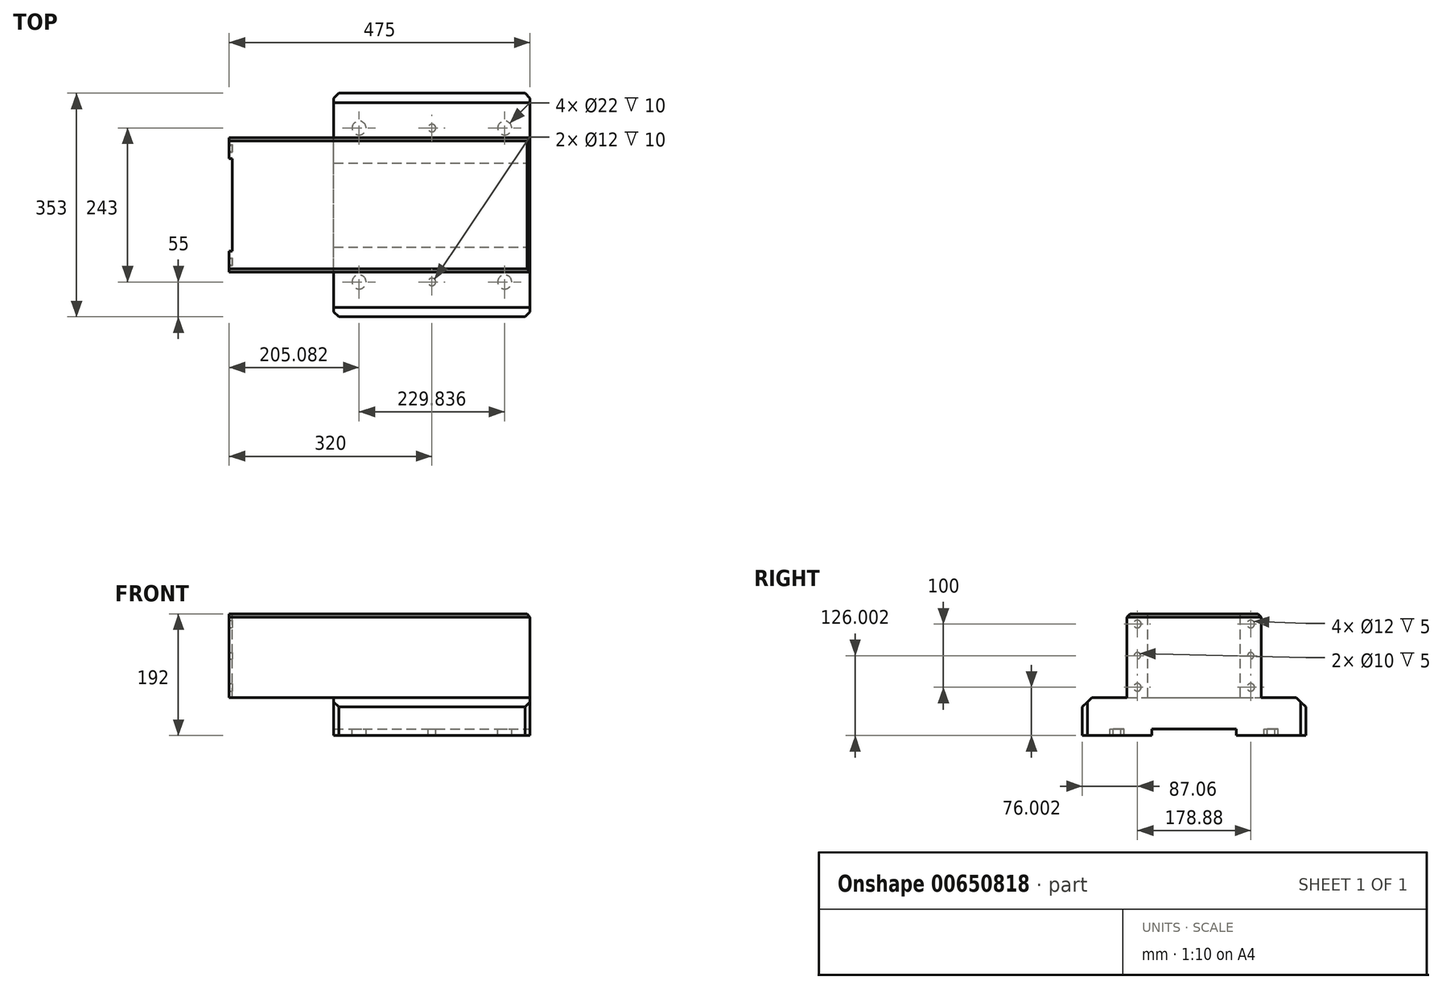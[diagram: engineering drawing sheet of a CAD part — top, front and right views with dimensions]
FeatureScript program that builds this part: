
annotation { "Feature Type Name" : "Feature", "Feature Type Description" : "" }
export const myFeature = defineFeature(function(context is Context, id is Id, definition is map)
    precondition{}
    {
        {
            var Q0;
            Q0=qCreatedBy(makeId("Right.planeOp"),FACE);
            var sketch = newSketch(context, id + "F0", { "sketchPlane" : qUnion([Q0])});
            skLineSegment(sketch, "E0.bottom", {"start": v(-105.91, 36.32) * mm, "end": v(105.91, 36.32) * mm});
            skLineSegment(sketch, "E0.top", {"start": v(-105.91, -95.68) * mm, "end": v(105.91, -95.68) * mm});
            skLineSegment(sketch, "E0.left", {"start": v(-105.91, 36.32) * mm, "end": v(-105.91, -95.68) * mm});
            skLineSegment(sketch, "E0.right", {"start": v(105.92, 36.32) * mm, "end": v(105.92, -95.68) * mm});
            skLineSegment(sketch, "E1", {"start": v(0, 36.32) * mm, "end": v(0, -95.68) * mm, "construction": true});
            skSolve(sketch);
        }
        {
            var Q0;
            Q0 = qSketchRegion(id + "F0", true);
            extrude(context, id + "F1", {"entities" : qUnion([Q0]), "depth" : 310 * mm, "offsetDistance" : 25 * mm, "hasSecondDirection" : true, "secondDirectionOppositeDirection" : true, "secondDirectionDepth" : 160 * mm});
        }
        {
            var Q0;
            Q0=makeQuery(id+"F1.opExtrude","CAP_FACE",FACE,{"disambiguationData":[OSD([sQuery(id+"F0.wireOp",EDGE,"E0.bottom"),sQuery(id+"F0.wireOp",EDGE,"E0.top"),sQuery(id+"F0.wireOp",EDGE,"E0.left"),sQuery(id+"F0.wireOp",EDGE,"E0.right")])],"isStart":true});
            var sketch = newSketch(context, id + "F2", { "sketchPlane" : qUnion([Q0])});
            skLineSegment(sketch, "E2.bottom", {"start": v(-105.92, -95.68) * mm, "end": v(-72.97, -95.68) * mm});
            skLineSegment(sketch, "E2.top", {"start": v(-105.92, 36.32) * mm, "end": v(-72.97, 36.32) * mm});
            skLineSegment(sketch, "E2.left", {"start": v(-105.92, -95.68) * mm, "end": v(-105.92, 36.32) * mm});
            skLineSegment(sketch, "E2.right", {"start": v(-72.97, -95.68) * mm, "end": v(-72.97, 36.32) * mm});
            skCircle(sketch, "E3", {"center": v(-89.44, 20.32) * mm, "radius": 6 * mm});
            skCircle(sketch, "E4", {"center": v(-89.44, -29.68) * mm, "radius": 5 * mm});
            skLineSegment(sketch, "E5", {"start": v(-89.44, 36.32) * mm, "end": v(-89.44, -132.2) * mm, "construction": true});
            skLineSegment(sketch, "E6", {"start": v(-105.92, -29.68) * mm, "end": v(-72.97, -29.68) * mm, "construction": true});
            skCircle(sketch, "E7.MirrorC", {"center": v(-89.44, -79.68) * mm, "radius": 6 * mm});
            skLineSegment(sketch, "E8", {"start": v(0, 0) * mm, "end": v(0, -157.18) * mm, "construction": true});
            skLineSegment(sketch, "E9.MirrorCS", {"start": v(89.44, 36.32) * mm, "end": v(89.44, -132.2) * mm, "construction": true});
            skLineSegment(sketch, "E10.MirrorCS", {"start": v(105.92, -95.68) * mm, "end": v(72.97, -95.68) * mm});
            skLineSegment(sketch, "E11.MirrorCS", {"start": v(105.91, 36.32) * mm, "end": v(72.96, 36.32) * mm});
            skLineSegment(sketch, "E12.MirrorCS", {"start": v(105.92, -95.68) * mm, "end": v(105.92, 36.32) * mm});
            skLineSegment(sketch, "E13.MirrorCS", {"start": v(105.92, -29.68) * mm, "end": v(72.97, -29.68) * mm, "construction": true});
            skLineSegment(sketch, "E14.MirrorCS", {"start": v(72.97, -95.68) * mm, "end": v(72.97, 36.32) * mm});
            skCircle(sketch, "E15.MirrorC", {"center": v(89.44, -79.68) * mm, "radius": 6 * mm});
            skCircle(sketch, "E16.MirrorC", {"center": v(89.44, -29.68) * mm, "radius": 5 * mm});
            skCircle(sketch, "E17.MirrorC", {"center": v(89.44, 20.32) * mm, "radius": 6 * mm});
            skSolve(sketch);
        }
        {
            var Q0;
            Q0 = qSketchRegion(id + "F2", true);
            extrude(context, id + "F3", {"entities" : qUnion([Q0]), "operationType" : NewBodyOperationType.ADD, "depth" : 5 * mm, "offsetDistance" : 25 * mm});
        }
        {
            var Q0;
            Q0=makeQuery(id+"F1.opExtrude","CAP_EDGE",EDGE,{"disambiguationData":[OSD([sQuery(id+"F0.wireOp",EDGE,"E0.bottom")])],"isStart":false});
            var Q1;
            Q1=makeQuery(id+"F1.opExtrude","SWEPT_EDGE",EDGE,{"disambiguationData":[OSD([sQuery(id+"F0.wireOp",EDGE,"E0.bottom"),sQuery(id+"F0.wireOp",EDGE,"E0.left")])]});
            var Q2;
            Q2=makeQuery(id+"F1.opExtrude","SWEPT_EDGE",EDGE,{"disambiguationData":[OSD([sQuery(id+"F0.wireOp",EDGE,"E0.bottom"),sQuery(id+"F0.wireOp",EDGE,"E0.right")])]});
            chamfer(context, id + "F4", {"entities" : qUnion([Q0, Q1, Q2]), "width" : 5 * mm, "tangentPropagation" : true});
        }
        {
            var Q0;
            Q0=makeQuery(id+"F3.boolean.opBoolean","MERGE",FACE,{"derivedFrom":[makeQuery(id+"F1.opExtrude","SWEPT_FACE",FACE,{"disambiguationData":[OSD([sQuery(id+"F0.wireOp",EDGE,"E0.top")])]}),makeQuery(id+"F3.opExtrude","SWEPT_FACE",FACE,{"disambiguationData":[OSD([sQuery(id+"F2.wireOp",EDGE,"E2.bottom")])]}),makeQuery(id+"F3.opExtrude","SWEPT_FACE",FACE,{"disambiguationData":[OSD([sQuery(id+"F2.wireOp",EDGE,"E10.MirrorCS")])]})]});
            var sketch = newSketch(context, id + "F5", { "sketchPlane" : qUnion([Q0])});
            skLineSegment(sketch, "E18", {"start": v(0, 0) * mm, "end": v(310, 0) * mm, "construction": true});
            skLineSegment(sketch, "E19.bottom", {"start": v(0, 176.5) * mm, "end": v(310, 176.5) * mm});
            skLineSegment(sketch, "E19.top", {"start": v(0, -176.5) * mm, "end": v(310, -176.5) * mm});
            skLineSegment(sketch, "E19.left", {"start": v(0, 176.5) * mm, "end": v(0, -176.5) * mm});
            skLineSegment(sketch, "E19.right", {"start": v(310, 176.5) * mm, "end": v(310, -176.5) * mm});
            skPoint(sketch, "E19.middle", {"position": v(155, 0) * mm});
            skSolve(sketch);
        }
        {
            var Q0;
            Q0 = qSketchRegion(id + "F5", true);
            extrude(context, id + "F6", {"entities" : qUnion([Q0]), "operationType" : NewBodyOperationType.ADD, "depth" : 50 * mm, "offsetDistance" : 25 * mm});
        }
        {
            var Q0;
            Q0=makeQuery(id+"F6.opExtrude","CAP_EDGE",EDGE,{"disambiguationData":[OSD([sQuery(id+"F5.wireOp",EDGE,"E19.bottom")])],"isStart":true});
            var Q1;
            Q1=makeQuery(id+"F6.opExtrude","CAP_EDGE",EDGE,{"disambiguationData":[OSD([sQuery(id+"F5.wireOp",EDGE,"E19.top")])],"isStart":true});
            chamfer(context, id + "F7", {"entities" : qUnion([Q0, Q1]), "width" : 15 * mm, "tangentPropagation" : true});
        }
        {
            var Q0;
            Q0=makeQuery(id+"F6.opExtrude","CAP_FACE",FACE,{"disambiguationData":[OSD([sQuery(id+"F5.wireOp",EDGE,"E19.bottom"),sQuery(id+"F5.wireOp",EDGE,"E19.top"),sQuery(id+"F5.wireOp",EDGE,"E19.left"),sQuery(id+"F5.wireOp",EDGE,"E19.right")])],"isStart":false});
            var sketch = newSketch(context, id + "F8", { "sketchPlane" : qUnion([Q0])});
            skLineSegment(sketch, "E20.bottom", {"start": v(0, 176.5) * mm, "end": v(310, 176.5) * mm});
            skLineSegment(sketch, "E20.top", {"start": v(0, 66.5) * mm, "end": v(310, 66.5) * mm});
            skLineSegment(sketch, "E20.left", {"start": v(0, 176.5) * mm, "end": v(0, 66.5) * mm});
            skLineSegment(sketch, "E20.right", {"start": v(310, 176.5) * mm, "end": v(310, 66.5) * mm});
            skLineSegment(sketch, "E21.MirrorCS", {"start": v(0, -66.5) * mm, "end": v(310, -66.5) * mm});
            skLineSegment(sketch, "E22.MirrorCS", {"start": v(0, -176.5) * mm, "end": v(310, -176.5) * mm});
            skLineSegment(sketch, "E23.MirrorCS", {"start": v(310, -176.5) * mm, "end": v(310, -66.5) * mm});
            skLineSegment(sketch, "E24.MirrorCS", {"start": v(0, -176.5) * mm, "end": v(0, -66.5) * mm});
            skCircle(sketch, "E25", {"center": v(40.08, 121.5) * mm, "radius": 11 * mm});
            skPoint(sketch, "E25.centerSnap0", {"position": v(0, 121.5) * mm});
            skCircle(sketch, "E26", {"center": v(155, 121.5) * mm, "radius": 6 * mm});
            skPoint(sketch, "E26.centerSnap0", {"position": v(155, 176.5) * mm});
            skLineSegment(sketch, "E27", {"start": v(155, 176.5) * mm, "end": v(155, 16.17) * mm, "construction": true});
            skCircle(sketch, "E28.MirrorC", {"center": v(269.92, 121.5) * mm, "radius": 11 * mm});
            skCircle(sketch, "E29.MirrorC", {"center": v(40.08, -121.5) * mm, "radius": 11 * mm});
            skCircle(sketch, "E30.MirrorC", {"center": v(155, -121.5) * mm, "radius": 6 * mm});
            skCircle(sketch, "E31.MirrorC", {"center": v(269.92, -121.5) * mm, "radius": 11 * mm});
            skSolve(sketch);
        }
        {
            var Q0;
            Q0 = qSketchRegion(id + "F8", true);
            extrude(context, id + "F9", {"entities" : qUnion([Q0]), "operationType" : NewBodyOperationType.ADD, "depth" : 10 * mm, "offsetDistance" : 25 * mm});
        }
        {
            var Q0;
            Q0=makeQuery(id+"F9.boolean.opBoolean","MERGE",EDGE,{"derivedFrom":[makeQuery(id+"F6.opExtrude","SWEPT_EDGE",EDGE,{"disambiguationData":[OSD([sQuery(id+"F5.wireOp",EDGE,"E19.bottom"),sQuery(id+"F5.wireOp",EDGE,"E19.left")])]}),makeQuery(id+"F9.opExtrude","SWEPT_EDGE",EDGE,{"disambiguationData":[OSD([sQuery(id+"F8.wireOp",EDGE,"E20.bottom"),sQuery(id+"F8.wireOp",EDGE,"E20.left")])]})]});
            var Q1;
            Q1=makeQuery(id+"F9.boolean.opBoolean","MERGE",EDGE,{"derivedFrom":[makeQuery(id+"F6.opExtrude","SWEPT_EDGE",EDGE,{"disambiguationData":[OSD([sQuery(id+"F5.wireOp",EDGE,"E19.top"),sQuery(id+"F5.wireOp",EDGE,"E19.left")])]}),makeQuery(id+"F9.opExtrude","SWEPT_EDGE",EDGE,{"disambiguationData":[OSD([sQuery(id+"F8.wireOp",EDGE,"E22.MirrorCS"),sQuery(id+"F8.wireOp",EDGE,"E24.MirrorCS")])]})]});
            var Q2;
            Q2=makeQuery(id+"F9.boolean.opBoolean","MERGE",EDGE,{"derivedFrom":[makeQuery(id+"F6.opExtrude","SWEPT_EDGE",EDGE,{"disambiguationData":[OSD([sQuery(id+"F5.wireOp",EDGE,"E19.top"),sQuery(id+"F5.wireOp",EDGE,"E19.right")])]}),makeQuery(id+"F9.opExtrude","SWEPT_EDGE",EDGE,{"disambiguationData":[OSD([sQuery(id+"F8.wireOp",EDGE,"E22.MirrorCS"),sQuery(id+"F8.wireOp",EDGE,"E23.MirrorCS")])]})]});
            var Q3;
            Q3=makeQuery(id+"F9.boolean.opBoolean","MERGE",EDGE,{"derivedFrom":[makeQuery(id+"F6.opExtrude","SWEPT_EDGE",EDGE,{"disambiguationData":[OSD([sQuery(id+"F5.wireOp",EDGE,"E19.bottom"),sQuery(id+"F5.wireOp",EDGE,"E19.right")])]}),makeQuery(id+"F9.opExtrude","SWEPT_EDGE",EDGE,{"disambiguationData":[OSD([sQuery(id+"F8.wireOp",EDGE,"E20.bottom"),sQuery(id+"F8.wireOp",EDGE,"E20.right")])]})]});
            chamfer(context, id + "F10", {"entities" : qUnion([Q0, Q1, Q2, Q3]), "width" : 8 * mm, "tangentPropagation" : true});
        }
    });
